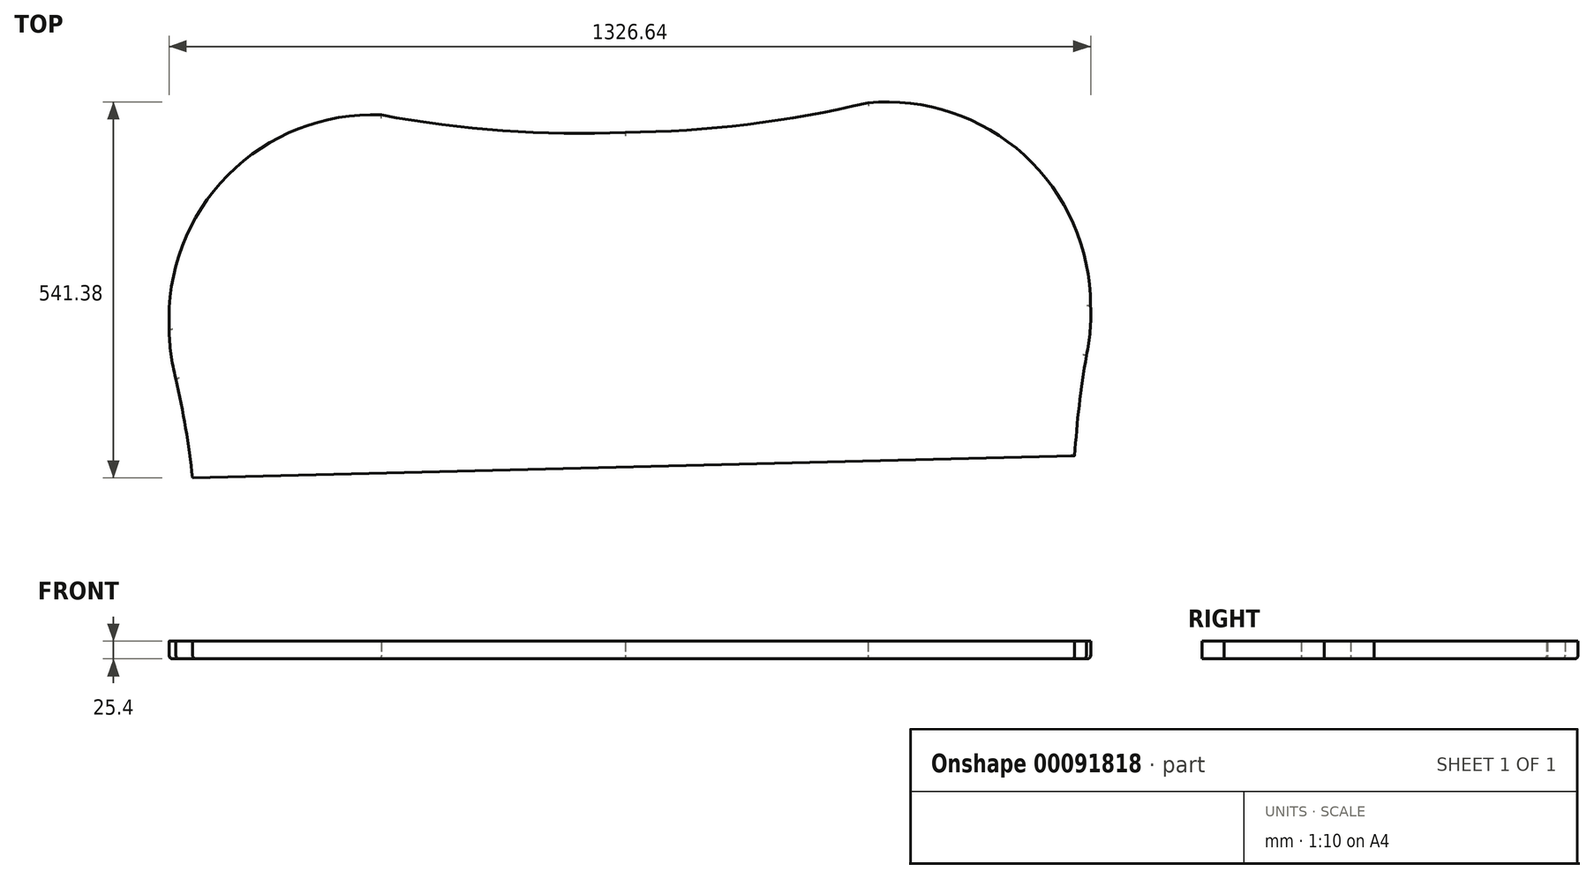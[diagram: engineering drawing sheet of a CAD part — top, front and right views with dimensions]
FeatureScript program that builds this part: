
annotation { "Feature Type Name" : "Feature", "Feature Type Description" : "" }
export const myFeature = defineFeature(function(context is Context, id is Id, definition is map)
    precondition{}
    {
        {
            var Q0;
            Q0=qCreatedBy(makeId("Top.planeOp"),FACE);
            var sketch = newSketch(context, id + "F0", { "sketchPlane" : qUnion([Q0])});
            skLineSegment(sketch, "E0", {"start": v(-561.67, -214.3) * mm, "end": v(707.93, -182.24) * mm});
            skLineSegment(sketch, "E1", {"start": v(73.13, -198.27) * mm, "end": v(60.97, 283.02) * mm});
            skArc(sketch, "E2", {"start": v(-290.24, 308.12) * mm, "mid": v(-115.34, 285.67) * mm, "end": v(60.97, 283.02) * mm});
            skArc(sketch, "E3", {"start": v(-290.24, 308.12) * mm, "mid": v(-510.85, 221.48) * mm, "end": v(-595.24, 0) * mm});
            skArc(sketch, "E4", {"start": v(-561.67, -214.3) * mm, "mid": v(-571.73, -142.47) * mm, "end": v(-585.7, -71.29) * mm});
            skArc(sketch, "E5", {"start": v(-595.24, 0) * mm, "mid": v(-592.87, -35.97) * mm, "end": v(-585.7, -71.29) * mm});
            skArc(sketch, "E6.MirrorCS", {"start": v(410.47, 325.82) * mm, "mid": v(236.93, 294.57) * mm, "end": v(60.97, 283.02) * mm});
            skArc(sketch, "E7.MirrorCS", {"start": v(410.47, 325.82) * mm, "mid": v(635.17, 250.42) * mm, "end": v(730.64, 33.48) * mm});
            skArc(sketch, "E8.MirrorCS", {"start": v(730.64, 33.48) * mm, "mid": v(730.09, -2.56) * mm, "end": v(724.7, -38.2) * mm});
            skArc(sketch, "E9.MirrorCS", {"start": v(707.93, -182.24) * mm, "mid": v(714.35, -109.99) * mm, "end": v(724.7, -38.2) * mm});
            skSolve(sketch);
        }
        {
            var Q0;
            {var subQ0=sQuery(id+"F0.wireOp",EDGE,"E1");Q0=makeQuery(id+"F0.imprint","IMPRINT",FACE,{"disambiguationData":[TD([[makeQuery(id+"F0.imprint","IMPRINT",EDGE,{"derivedFrom":subQ0}),1.0]])]});}
            var Q1;
            {var subQ2=sQuery(id+"F0.wireOp",EDGE,"E1");Q1=makeQuery(id+"F0.imprint","IMPRINT",FACE,{"disambiguationData":[TD([[makeQuery(id+"F0.imprint","IMPRINT",EDGE,{"derivedFrom":subQ2}),-1.0]])]});}
            extrude(context, id + "F1", {"entities" : qUnion([Q0, Q1]), "depth" : 25.4 * mm});
        }
        {
            var Q0;
            Q0=makeQuery(id+"F1.opExtrude","CAP_EDGE",EDGE,{"disambiguationData":[OSD([sQuery(id+"F0.wireOp",EDGE,"E2")])],"isStart":true});
            var Q1;
            Q1=makeQuery(id+"F1.opExtrude","CAP_EDGE",EDGE,{"disambiguationData":[OSD([sQuery(id+"F0.wireOp",EDGE,"E6.MirrorCS")])],"isStart":true});
            var Q2;
            Q2=makeQuery(id+"F1.opExtrude","CAP_EDGE",EDGE,{"disambiguationData":[OSD([sQuery(id+"F0.wireOp",EDGE,"E7.MirrorCS")])],"isStart":true});
            var Q3;
            Q3=makeQuery(id+"F1.opExtrude","CAP_EDGE",EDGE,{"disambiguationData":[OSD([sQuery(id+"F0.wireOp",EDGE,"E3")])],"isStart":true});
            var Q4;
            Q4=makeQuery(id+"F1.opExtrude","CAP_EDGE",EDGE,{"disambiguationData":[OSD([sQuery(id+"F0.wireOp",EDGE,"E8.MirrorCS")])],"isStart":true});
            var Q5;
            Q5=makeQuery(id+"F1.opExtrude","CAP_EDGE",EDGE,{"disambiguationData":[OSD([sQuery(id+"F0.wireOp",EDGE,"E9.MirrorCS")])],"isStart":true});
            var Q6;
            Q6=makeQuery(id+"F1.opExtrude","CAP_EDGE",EDGE,{"disambiguationData":[OSD([sQuery(id+"F0.wireOp",EDGE,"E5")])],"isStart":true});
            var Q7;
            Q7=makeQuery(id+"F1.opExtrude","CAP_EDGE",EDGE,{"disambiguationData":[OSD([sQuery(id+"F0.wireOp",EDGE,"E4")])],"isStart":true});
            fillet(context, id + "F2", {"entities" : qUnion([Q0, Q1, Q2, Q3, Q4, Q5, Q6, Q7]), "radius" : 5.08 * mm, "tangentPropagation" : true, "allowEdgeOverflow" : false});
        }
    });
